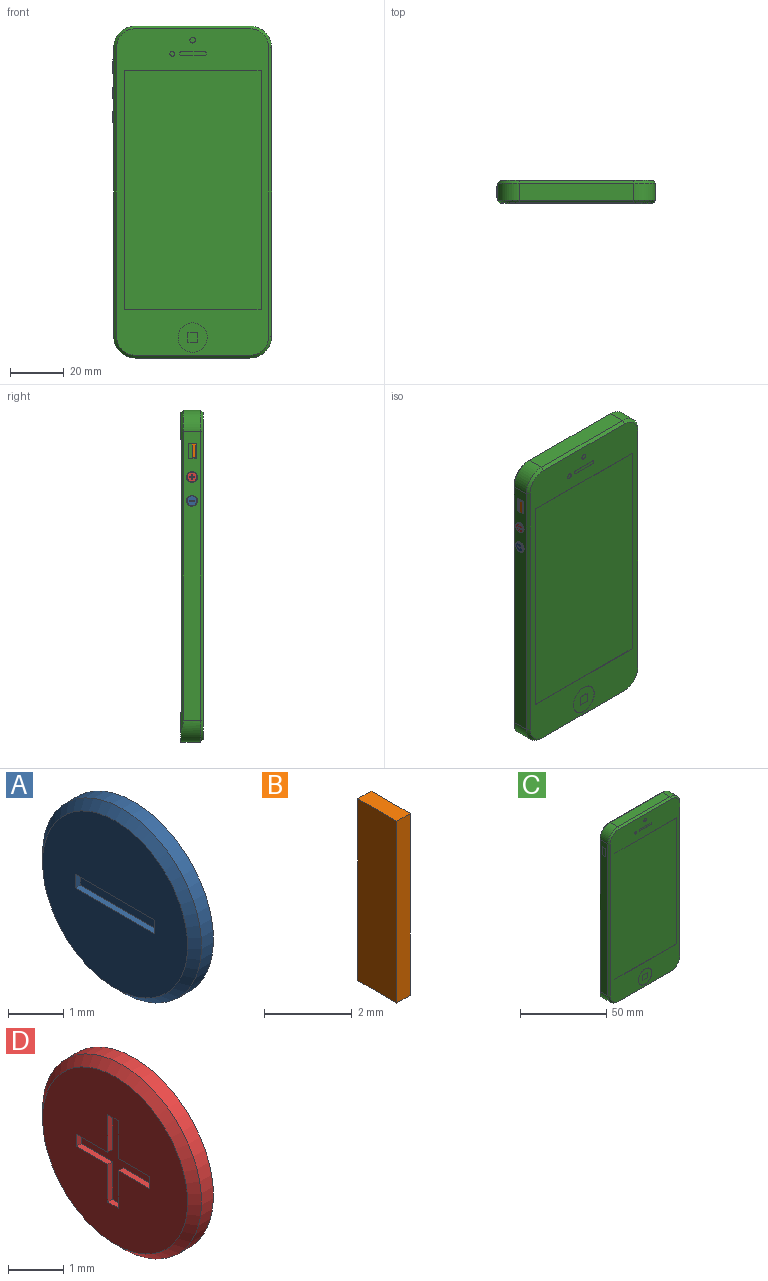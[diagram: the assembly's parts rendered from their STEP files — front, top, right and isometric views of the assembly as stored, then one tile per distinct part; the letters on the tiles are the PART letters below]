
ASSEMBLY  parts=4 mates=3
PART A: 9 faces, bbox 0.5x4.1x4.1 mm
  f0: plane 3.71x3.71mm, normal (-1,0,0), area 10.2mm2, adj f3,f4,f5,f6,f7
  f1: cylinder r=2.03mm len=4.06mm, axis (1,0,0), area 3.9mm2, adj f2,f3
  f2: plane 4.06x4.06mm, normal (1,0,0), area 13mm2, adj f1
  f3: cone r=1.85mm half-angle=45deg, axis (1,0,0), area 3.1mm2, adj f0,f1
  f4: plane 2.03x0.13mm, normal (0,0,-1), area 0.3mm2, adj f0,f5,f7,f8
  f5: plane 0.3x0.13mm, normal (0,-1,0), area 0mm2, adj f0,f4,f6,f8
  f6: plane 2.03x0.13mm, normal (0,0,1), area 0.3mm2, adj f0,f5,f7,f8
  f7: plane 0.3x0.13mm, normal (0,1,0), area 0mm2, adj f0,f4,f6,f8
  f8: plane 2.03x0.3mm, normal (-1,0,0), area 0.6mm2, adj f4,f5,f6,f7
PART B: 6 faces, bbox 0.4x1.3x5.1 mm
  f0: plane 1.25x0.43mm, normal (0,0,1), area 0.5mm2, adj f1,f3,f4,f5
  f1: plane 5.07x0.43mm, normal (0,1,0), area 2.2mm2, adj f0,f2,f4,f5
  f2: plane 1.25x0.43mm, normal (0,0,-1), area 0.5mm2, adj f1,f3,f4,f5
  f3: plane 5.07x0.43mm, normal (0,-1,0), area 2.2mm2, adj f0,f2,f4,f5
  f4: plane 5.07x1.25mm, normal (-1,0,0), area 6.4mm2, adj f0,f1,f2,f3
  f5: plane 5.07x1.25mm, normal (1,0,0), area 6.4mm2, adj f0,f1,f2,f3
PART C: 120 faces, bbox 58.9x8.4x124 mm
  f0: plane 107.7x6.35mm, normal (-1,0,0), area 667.6mm2, adj f7,f8,f53,f62,f115,f116,f117,f118
  f1: plane 56.9x10.92mm, normal (0,1,0), area 604.2mm2, adj f8,f9,f10,f48,f58,f62
  f2: plane 56.9x9.91mm, normal (0,1,0), area 513.2mm2, adj f36,f37,f38,f39,f41,f44,f47,f58
  f3: plane 121.92x56.9mm, normal (0,-1,0), area 2216.8mm2, adj f15,f18,f19,f20,f21,f23,f24,f25
  f4: plane 107.7x6.35mm, normal (1,0,0), area 683.9mm2, adj f5,f10,f54,f58
  f5: cylinder r=8.13mm len=8.13mm, axis (0,1,0), area 81.1mm2, adj f4,f6,f52,f59
  f6: plane 42.67x6.35mm, normal (0,0,1), area 271mm2, adj f5,f7,f50,f60
  f7: cylinder r=8.13mm len=8.13mm, axis (0,1,0), area 81.1mm2, adj f0,f6,f51,f61
  f8: cylinder r=8.13mm len=8.13mm, axis (0,1,0), area 91.3mm2, adj f0,f1,f9,f55,f62
  f9: plane 42.67x7.37mm, normal (0,0,-1), area 302.5mm2, adj f1,f8,f10,f57,f63,f65,f67,f69
  f10: cylinder r=8.13mm len=8.13mm, axis (0,1,0), area 91.3mm2, adj f1,f4,f9,f56,f58
  f11: plane 3.56x0.14mm, normal (1,0,0), area 0.5mm2, adj f12,f14,f16,f17
  f12: plane 3.56x0.14mm, normal (0,0,-1), area 0.5mm2, adj f11,f13,f16,f17
  f13: plane 3.56x0.14mm, normal (-1,0,0), area 0.5mm2, adj f12,f14,f16,f17
  f14: plane 3.56x0.14mm, normal (0,0,1), area 0.5mm2, adj f11,f13,f16,f17
  f15: cylinder r=5.46mm len=10.92mm, axis (0,-1,0), area 4.7mm2, adj f3,f16
  f16: plane 10.92x10.92mm, normal (0,-1,0), area 81mm2, adj f11,f12,f13,f14,f15
  f17: plane 3.56x3.56mm, normal (0,-1,0), area 12.6mm2, adj f11,f12,f13,f14
  f18: plane 51.05x0.14mm, normal (0,0,-1), area 7mm2, adj f3,f19,f21,f22
  f19: plane 89.41x0.14mm, normal (1,0,0), area 12.3mm2, adj f3,f18,f20,f22
  f20: plane 51.05x0.14mm, normal (0,0,1), area 7mm2, adj f3,f19,f21,f22
  f21: plane 89.41x0.14mm, normal (-1,0,0), area 12.3mm2, adj f3,f18,f20,f22
  f22: plane 89.41x51.05mm, normal (0,-1,0), area 4564.6mm2, adj f18,f19,f20,f21
  f23: plane 9.14x0.14mm, normal (0,0,-1), area 1.3mm2, adj f3,f24,f30,f31
  f24: cylinder r=0.38mm len=0.38mm, axis (0,-1,0), area 0.1mm2, adj f3,f23,f25,f31
  f25: plane 0.51x0.14mm, normal (1,0,0), area 0.1mm2, adj f3,f24,f26,f31
  f26: cylinder r=0.38mm len=0.38mm, axis (0,-1,0), area 0.1mm2, adj f3,f25,f27,f31
  f27: plane 9.14x0.14mm, normal (0,0,1), area 1.3mm2, adj f3,f26,f28,f31
  f28: cylinder r=0.38mm len=0.38mm, axis (0,-1,0), area 0.1mm2, adj f3,f27,f29,f31
  f29: plane 0.51x0.14mm, normal (-1,0,0), area 0.1mm2, adj f3,f28,f30,f31
  f30: cylinder r=0.38mm len=0.38mm, axis (0,-1,0), area 0.1mm2, adj f3,f23,f29,f31
  f31: plane 9.91x1.27mm, normal (0,-1,0), area 12.5mm2, adj f23,f24,f25,f26,f27,f28,f29,f30
  f32: cylinder r=0.89mm len=1.78mm, axis (0,-1,0), area 0.8mm2, adj f3,f33
  f33: plane 1.78x1.78mm, normal (0,-1,0), area 2.5mm2, adj f32
  f34: cylinder r=1.02mm len=2.03mm, axis (0,-1,0), area 0.9mm2, adj f3,f35
  f35: plane 2.03x2.03mm, normal (0,-1,0), area 3.2mm2, adj f34
  f36: plane 0.76x0.13mm, normal (0,0,-1), area 0.1mm2, adj f2,f37,f39,f40
  f37: plane 0.25x0.13mm, normal (-1,0,0), area 0mm2, adj f2,f36,f38,f40
  f38: plane 0.76x0.13mm, normal (0,0,1), area 0.1mm2, adj f2,f37,f39,f40
  f39: plane 0.25x0.13mm, normal (1,0,0), area 0mm2, adj f2,f36,f38,f40
  f40: plane 0.76x0.25mm, normal (0,1,0), area 0.2mm2, adj f36,f37,f38,f39
  f41: cylinder r=1.4mm len=2.79mm, axis (0,1,0), area 1.1mm2, adj f2,f42
  f42: plane 2.79x2.79mm, normal (0,1,0), area 6.1mm2, adj f41
  f43: cylinder r=1.78mm len=3.56mm, axis (0,1,0), area 1.4mm2, adj f45,f46
  f44: cylinder r=2.67mm len=5.33mm, axis (0,1,0), area 2.1mm2, adj f2,f45
  f45: plane 5.33x5.33mm, normal (0,1,0), area 12.4mm2, adj f43,f44
  f46: plane 3.56x3.56mm, normal (0,1,0), area 9.9mm2, adj f43
  f47: plane 57.15x0.13mm, normal (0,0,-1), area 7.2mm2, adj f2,f49,f58,f62
  f48: plane 57.15x0.13mm, normal (0,0,1), area 7.2mm2, adj f1,f49,f58,f62
  f49: plane 102.11x57.15mm, normal (0,1,0), area 5835.5mm2, adj f47,f48,f58,f62
  f50: plane 42.67x1.02mm, normal (0,-0.71,0.71), area 61.3mm2, adj f3,f6,f51,f52
  f51: cone r=7.11mm half-angle=45deg, axis (0,1,0), area 17.2mm2, adj f3,f7,f50,f53
  f52: cone r=7.11mm half-angle=45deg, axis (0,1,0), area 17.2mm2, adj f3,f5,f50,f54
  f53: plane 107.7x1.02mm, normal (-0.71,-0.71,0), area 154.7mm2, adj f0,f3,f51,f55
  f54: plane 107.7x1.02mm, normal (0.71,-0.71,0), area 154.7mm2, adj f3,f4,f52,f56
  f55: cone r=7.11mm half-angle=45deg, axis (0,1,0), area 17.2mm2, adj f3,f8,f53,f57
  f56: cone r=7.11mm half-angle=45deg, axis (0,1,0), area 17.2mm2, adj f3,f10,f54,f57
  f57: plane 42.67x1.02mm, normal (0,-0.71,-0.71), area 61.3mm2, adj f3,f9,f55,f56
  f58: plane 111.63x1.02mm, normal (0.71,0.71,0), area 140.2mm2, adj f1,f2,f4,f10,f47,f48,f49,f59
  f59: cone r=8.13mm half-angle=45deg, axis (0,-1,0), area 17.2mm2, adj f2,f5,f58,f60
  f60: plane 42.67x1.02mm, normal (0,0.71,0.71), area 61.3mm2, adj f2,f6,f59,f61
  f61: cone r=8.13mm half-angle=45deg, axis (0,-1,0), area 17.2mm2, adj f2,f7,f60,f62
  f62: plane 111.63x1.02mm, normal (-0.71,0.71,0), area 140.2mm2, adj f0,f1,f2,f8,f47,f48,f49,f61
  f63: cylinder r=0.38mm len=1.27mm, axis (0,0,-1), area 3mm2, adj f9,f64
  f64: plane 0.76x0.76mm, normal (0,0,-1), area 0.5mm2, adj f63
  f65: cylinder r=0.38mm len=1.27mm, axis (0,0,-1), area 3mm2, adj f9,f66
  f66: plane 0.76x0.76mm, normal (0,0,-1), area 0.5mm2, adj f65
  f67: cylinder r=0.38mm len=1.27mm, axis (0,0,-1), area 3mm2, adj f9,f68
  f68: plane 0.76x0.76mm, normal (0,0,-1), area 0.5mm2, adj f67
  f69: cylinder r=0.38mm len=1.27mm, axis (0,0,-1), area 3mm2, adj f9,f70
  f70: plane 0.76x0.76mm, normal (0,0,-1), area 0.5mm2, adj f69
  f71: cylinder r=0.38mm len=1.27mm, axis (0,0,-1), area 3mm2, adj f9,f72
  f72: plane 0.76x0.76mm, normal (0,0,-1), area 0.5mm2, adj f71
  f73: cylinder r=0.38mm len=1.27mm, axis (0,0,-1), area 3mm2, adj f9,f74
  f74: plane 0.76x0.76mm, normal (0,0,-1), area 0.5mm2, adj f73
  f75: cylinder r=0.38mm len=1.27mm, axis (0,0,-1), area 3mm2, adj f9,f76
  f76: plane 0.76x0.76mm, normal (0,0,-1), area 0.5mm2, adj f75
  f77: cylinder r=0.38mm len=1.27mm, axis (0,0,-1), area 3mm2, adj f9,f78
  f78: plane 0.76x0.76mm, normal (0,0,-1), area 0.5mm2, adj f77
  f79: cylinder r=0.38mm len=1.27mm, axis (0,0,-1), area 3mm2, adj f9,f80
  f80: plane 0.76x0.76mm, normal (0,0,-1), area 0.5mm2, adj f79
  f81: cylinder r=0.38mm len=1.27mm, axis (0,0,-1), area 3mm2, adj f9,f82
  f82: plane 0.76x0.76mm, normal (0,0,-1), area 0.5mm2, adj f81
  f83: cylinder r=0.38mm len=1.27mm, axis (0,0,-1), area 3mm2, adj f9,f84
  f84: plane 0.76x0.76mm, normal (0,0,-1), area 0.5mm2, adj f83
  f85: cylinder r=0.38mm len=1.27mm, axis (0,0,-1), area 3mm2, adj f9,f86
  f86: plane 0.76x0.76mm, normal (0,0,-1), area 0.5mm2, adj f85
  f87: cylinder r=0.38mm len=1.27mm, axis (0,0,-1), area 3mm2, adj f9,f88
  f88: plane 0.76x0.76mm, normal (0,0,-1), area 0.5mm2, adj f87
  f89: cylinder r=0.38mm len=1.27mm, axis (0,0,-1), area 3mm2, adj f9,f90
  f90: plane 0.76x0.76mm, normal (0,0,-1), area 0.5mm2, adj f89
  f91: cylinder r=0.38mm len=1.27mm, axis (0,0,-1), area 3mm2, adj f9,f92
  f92: plane 0.76x0.76mm, normal (0,0,-1), area 0.5mm2, adj f91
  f93: cylinder r=0.38mm len=1.27mm, axis (0,0,-1), area 3mm2, adj f9,f94
  f94: plane 0.76x0.76mm, normal (0,0,-1), area 0.5mm2, adj f93
  f95: cylinder r=0.38mm len=1.27mm, axis (0,0,-1), area 3mm2, adj f9,f96
  f96: plane 0.76x0.76mm, normal (0,0,-1), area 0.5mm2, adj f95
  f97: cylinder r=0.38mm len=1.27mm, axis (0,0,-1), area 3mm2, adj f9,f98
  f98: plane 0.76x0.76mm, normal (0,0,-1), area 0.5mm2, adj f97
  f99: cylinder r=0.38mm len=1.27mm, axis (0,0,-1), area 3mm2, adj f9,f100
  f100: plane 0.76x0.76mm, normal (0,0,-1), area 0.5mm2, adj f99
  f101: cylinder r=0.38mm len=1.27mm, axis (0,0,-1), area 3mm2, adj f9,f102
  f102: plane 0.76x0.76mm, normal (0,0,-1), area 0.5mm2, adj f101
  f103: cylinder r=0.38mm len=1.27mm, axis (0,0,-1), area 3mm2, adj f9,f104
  f104: plane 0.76x0.76mm, normal (0,0,-1), area 0.5mm2, adj f103
  f105: cylinder r=0.38mm len=1.27mm, axis (0,0,-1), area 3mm2, adj f9,f106
  f106: plane 0.76x0.76mm, normal (0,0,-1), area 0.5mm2, adj f105
  f107: cylinder r=0.38mm len=1.27mm, axis (0,0,-1), area 3mm2, adj f9,f108
  f108: plane 0.76x0.76mm, normal (0,0,-1), area 0.5mm2, adj f107
  f109: cylinder r=0.38mm len=1.27mm, axis (0,0,-1), area 3mm2, adj f9,f110
  f110: plane 0.76x0.76mm, normal (0,0,-1), area 0.5mm2, adj f109
  f111: cylinder r=0.38mm len=1.27mm, axis (0,0,-1), area 3mm2, adj f9,f112
  f112: plane 0.76x0.76mm, normal (0,0,-1), area 0.5mm2, adj f111
  f113: cylinder r=0.38mm len=1.27mm, axis (0,0,-1), area 3mm2, adj f9,f114
  f114: plane 0.76x0.76mm, normal (0,0,-1), area 0.5mm2, adj f113
  f115: plane 2.84x0.13mm, normal (0,0,-1), area 0.4mm2, adj f0,f116,f118,f119
  f116: plane 5.72x0.13mm, normal (0,-1,0), area 0.7mm2, adj f0,f115,f117,f119
  f117: plane 2.84x0.13mm, normal (0,0,1), area 0.4mm2, adj f0,f116,f118,f119
  f118: plane 5.72x0.13mm, normal (0,1,0), area 0.7mm2, adj f0,f115,f117,f119
  f119: plane 5.72x2.84mm, normal (-1,0,0), area 16.2mm2, adj f115,f116,f117,f118
PART D: 17 faces, bbox 0.5x4.1x4.1 mm
  f0: plane 3.71x3.71mm, normal (-1,0,0), area 9.8mm2, adj f3,f4,f5,f6,f7,f8,f9,f10
  f1: cylinder r=2.03mm len=4.06mm, axis (1,0,0), area 3.9mm2, adj f2,f3
  f2: plane 4.06x4.06mm, normal (1,0,0), area 13mm2, adj f1
  f3: cone r=1.85mm half-angle=45deg, axis (1,0,0), area 3.1mm2, adj f0,f1
  f4: plane 0.8x0.13mm, normal (0,0,-1), area 0.1mm2, adj f0,f5,f15,f16
  f5: plane 0.84x0.13mm, normal (0,1,0), area 0.1mm2, adj f0,f4,f6,f16
  f6: plane 0.27x0.13mm, normal (0,0,-1), area 0mm2, adj f0,f5,f7,f16
  f7: plane 0.84x0.13mm, normal (0,-1,0), area 0.1mm2, adj f0,f6,f8,f16
  f8: plane 0.8x0.13mm, normal (0,0,-1), area 0.1mm2, adj f0,f7,f9,f16
  f9: plane 0.27x0.13mm, normal (0,-1,0), area 0mm2, adj f0,f8,f10,f16
  f10: plane 0.8x0.13mm, normal (0,0,1), area 0.1mm2, adj f0,f9,f11,f16
  f11: plane 0.83x0.13mm, normal (0,-1,0), area 0.1mm2, adj f0,f10,f12,f16
  f12: plane 0.27x0.13mm, normal (0,0,1), area 0mm2, adj f0,f11,f13,f16
  f13: plane 0.83x0.13mm, normal (0,1,0), area 0.1mm2, adj f0,f12,f14,f16
  f14: plane 0.8x0.13mm, normal (0,0,1), area 0.1mm2, adj f0,f13,f15,f16
  f15: plane 0.27x0.13mm, normal (0,1,0), area 0mm2, adj f0,f4,f14,f16
  f16: plane 1.94x1.88mm, normal (-1,0,0), area 1mm2, adj f4,f5,f6,f7,f8,f9,f10,f11
PLACE A t=(-16.75,77.02,-23.96)mm
PLACE B rot(axis=(0,1,0),180deg) t=(-16.93,76.26,191.9)mm
PLACE C t=(-16.75,77.2,-25.62)mm
PLACE D t=(-16.75,77.16,-24.72)mm
MATE fastened A.f1 <-> C.f0  axis (1,0,0) through (-16.75,73.01,64.43)mm
MATE fastened C.f0 <-> D.f2  axis (-1,0,0) through (-16.75,73.01,35.22)mm
MATE slider B.f3 <-> C.f118  axis (0,-1,0) through (-16.62,71.69,83.12)mm
